# Revit family: PC6060
name_source: partatom
category: Luminarias
units: mm (PartAtom-declared; Revit-internal decimal feet)

## family parameters
Compartido = Sí
Corte con vacíos al cargar = No
Cota de conector redondo = Diámetro de uso
Origen de luz = No
Punto de cálculo de habitación = No
Se basa en plano de trabajo = Sí
Siempre vertical = No
Tipo de pieza = Normal

## types (1)
- PERFIL_PC6060
    Descripción = PERFIL PARA SUSPENDER DE ALUMINIO CIRCULAR CON DIFUSOR LECHOSO, PARA ALOJAR TIRA LUMINOSA, PERFIL DE COLOCACION DE 39.1MM DE ANCHO. INSTALACION SOBRE SUPERFICIES, CUENTA CON PIEZAS DE SUJECION PARA DIRIGIR LA CANALETA Y DESPLAZARLA. IDEAL PARA ATENUAR EL BRILLO E INCORPORAR LA LUZ AL AMBIENTE.PRESENTACION DESDE 0.5 - 3 METROS, REQUEIRE ACCESORIOS COMO TAPA FINAL (CONSIDERAR 1 PAR POR SEGMENTO DE PERFIL) Y SET DE TENSORES (CONSIDERAR 3 PZAS POR SEGMENTO DE PERFIL).
    Elevación por defecto = 1219 mm
    Fabricante = BRILLANT
    Longitud = 1000 mm  [stored 3.28084 ft]
    Modelo = PC6060
    Set de Tensores 6060.2 = 3
    Tapa Final 6060.1 = 1

note: [stored X ft] marks values corroborated as IEEE doubles in the binary element streams (Revit-internal decimal feet)

## geometry (parser evidence)
native form markers: Blend x2
no freeform markers — native parametric forms only
